# Revit family: Bathtub-American_Standard-Coastal_Serin-2765.034
name_source: partatom
category: Plumbing Fixtures
revit_build: Autodesk Revit 2018 (Build: 20170223_1515(x64)
units: mm (PartAtom-declared; Revit-internal decimal feet)

## family parameters
Always vertical = No
Cut with Voids When Loaded = No
OmniClass Number = 23.45.05.14.21.11
OmniClass Title = Bath/Shower Units
Part Type = Normal
Room Calculation Point = No
Round Connector Dimension = Use Diameter
Shared = Yes
Work Plane-Based = Yes

## types (1)
- 2765.034
    Assembly Code = D2010510
    Body Material = Acrylic-American_Standard-020-High_Gloss_White
    CW Connection = No
    CWFU = 0
    Default Elevation = 23 5/8"
    Description = Coastal Serin 68.75 in. Acrylic Freestanding Soaker Bathtub in White
    HW Connection = No
    HWFU = 0
    Height = 23 5/8"
    IAPMO Compliance = Meets or Exceeds IAPMO Z124-2011, CSA B45.5-11
    Installation Type = Floor Mounted
    Length = 68 3/4"
    Manufacturer = American Standard
    Model = 2765.034
    Price = Prices may vary. Please consult Manufacturer Representative for most up-to-date price list.
    Product Documentation Link = https://www.americanstandard-us.com
    Product Page URL = https://www.americanstandard-us.com
    Revised Date = 03/26/2021
    Shipping Weight = 100 lb
    URL = https://www.americanstandard-us.com
    Vent Connection = No
    WFU = 4
    Warranty Information = Limited Lifetime Warranty
    Waste Connection = Yes
    Waste Connection Radius = 1 1/16"
    Water Connection Diameter = 2 1/8"
    Width = 31 1/4"
    cUPC Compliant = Yes

## geometry (parser evidence)
native form markers: Sweep x2
no freeform markers — native parametric forms only
